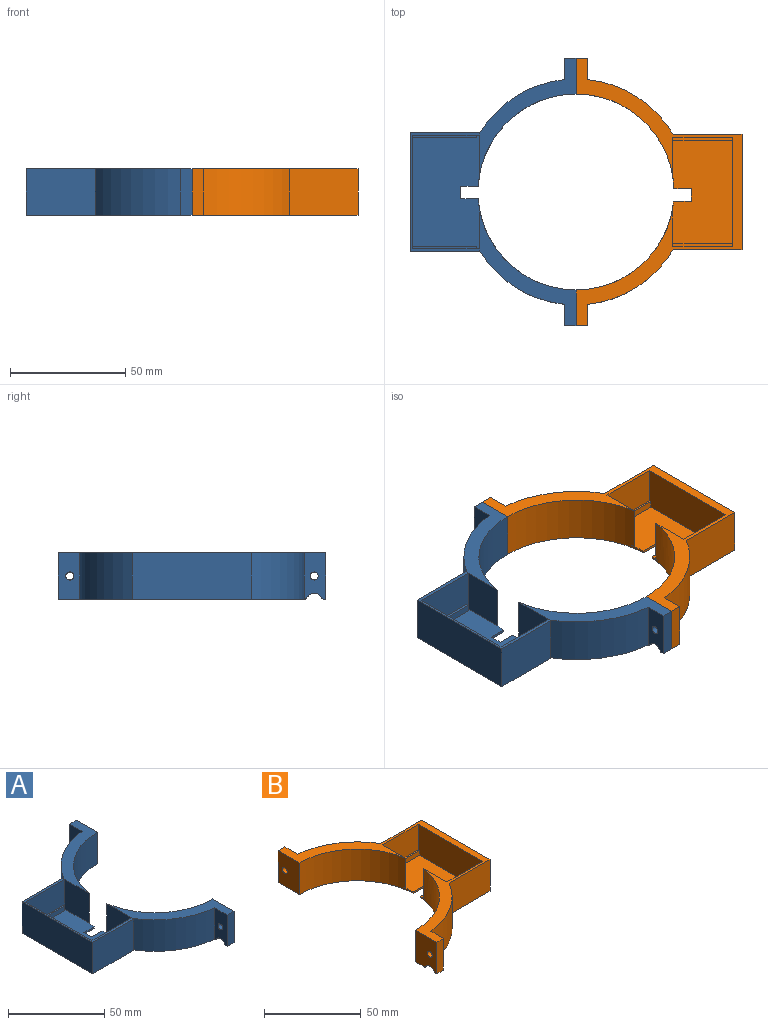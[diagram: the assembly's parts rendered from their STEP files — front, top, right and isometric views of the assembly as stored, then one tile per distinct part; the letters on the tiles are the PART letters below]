
ASSEMBLY  parts=2 mates=1
PART A: 38 faces, bbox 72x116x20 mm
  f0: plane 106.97x72mm, normal (0,0,-1), area 2259.8mm2, adj f1,f5,f6,f7,f8,f9,f10,f12
  f1: plane 20x9.26mm, normal (-1,0,0), area 163mm2, adj f0,f6,f11,f14,f32,f34,f35,f36
  f2: plane 49x29mm, normal (0,0,1), area 1319.7mm2, adj f3,f4,f5,f10,f20,f21,f22,f23
  f3: plane 49x19mm, normal (1,0,0), area 925mm2, adj f2,f4,f21,f27,f28,f30,f31,f32
  f4: plane 29x19mm, normal (0,-1,0), area 467mm2, adj f2,f3,f20,f26,f28,f32
  f5: cylinder r=42.5mm len=42.39mm, axis (0,0,1), area 1208.2mm2, adj f0,f2,f9,f22,f23,f32
  f6: cylinder r=49mm len=37mm, axis (0,0,1), area 908.9mm2, adj f0,f1,f15,f32
  f7: plane 20x15.5mm, normal (1,0,0), area 300.4mm2, adj f0,f10,f13,f32,f33
  f8: cylinder r=49mm len=37mm, axis (0,0,1), area 908.9mm2, adj f0,f12,f16,f32
  f9: plane 20x15.5mm, normal (1,0,0), area 287.9mm2, adj f0,f5,f11,f14,f32,f34,f35,f36
  f10: cylinder r=42.5mm len=42.43mm, axis (0,0,1), area 1208.7mm2, adj f0,f2,f7,f20,f24,f32
  f11: plane 5x0.97mm, normal (0,0,-1), area 4.8mm2, adj f1,f9,f14,f36
  f12: plane 20x9.26mm, normal (-1,0,0), area 175.5mm2, adj f0,f8,f13,f32,f33
  f13: plane 20x5mm, normal (0,1,0), area 100mm2, adj f0,f7,f12,f32
  f14: plane 20x5mm, normal (0,-1,0), area 100mm2, adj f1,f9,f11,f32
  f15: plane 20x0.76mm, normal (1,0,0), area 15.2mm2, adj f0,f6,f18,f32
  f16: plane 20x0.76mm, normal (1,0,0), area 15.2mm2, adj f0,f8,f19,f32
  f17: plane 52x20mm, normal (-1,0,0), area 1040mm2, adj f0,f18,f19,f32
  f18: plane 30x20mm, normal (0,-1,0), area 600mm2, adj f0,f15,f17,f32
  f19: plane 30x20mm, normal (0,1,0), area 600mm2, adj f0,f16,f17,f32
  f20: plane 19x18mm, normal (-1,0,0), area 342mm2, adj f2,f4,f10,f32
  f21: plane 29x19mm, normal (0,1,0), area 467mm2, adj f2,f3,f22,f29,f31,f32
  f22: plane 19x18mm, normal (-1,0,0), area 342mm2, adj f2,f5,f21,f32
  f23: plane 7.53x1mm, normal (0,1,0), area 7.5mm2, adj f0,f2,f5,f25
  f24: plane 7.5x1mm, normal (0,-1,0), area 7.5mm2, adj f0,f2,f10,f25
  f25: plane 5.5x1mm, normal (1,0,0), area 5.5mm2, adj f0,f2,f23,f24
  f26: plane 3x1mm, normal (1,0,0), area 3mm2, adj f2,f4,f27,f28
  f27: plane 28x3mm, normal (0,-1,0), area 84mm2, adj f2,f3,f26,f28
  f28: plane 28x1mm, normal (0,0,1), area 28mm2, adj f3,f4,f26,f27
  f29: plane 3x1mm, normal (1,0,0), area 3mm2, adj f2,f21,f30,f31
  f30: plane 28x3mm, normal (0,1,0), area 84mm2, adj f2,f3,f29,f31
  f31: plane 28x1mm, normal (0,0,1), area 28mm2, adj f3,f21,f29,f30
  f32: plane 116x72mm, normal (0,0,1), area 929.3mm2, adj f1,f3,f4,f5,f6,f7,f8,f9
  f33: cylinder r=1.75mm len=5mm, axis (-1,0,0), area 55mm2, adj f7,f12
  f34: cylinder r=1.75mm len=5mm, axis (-1,0,0), area 55mm2, adj f1,f9
  f35: cylinder r=3.5mm len=6.27mm, axis (1,0,0), area 38.9mm2, adj f1,f9,f36,f37
  f36: cylinder r=1mm len=5mm, axis (1,0,0), area 5.6mm2, adj f1,f9,f11,f35
  f37: cylinder r=1mm len=5mm, axis (1,0,0), area 5.6mm2, adj f0,f1,f9,f35
PART B: 34 faces, bbox 72x116x20 mm
  f0: plane 5x0.97mm, normal (0,0,-1), area 4.8mm2, adj f1,f8,f12,f33
  f1: plane 20x9.26mm, normal (1,0,0), area 163mm2, adj f0,f7,f11,f12,f25,f26,f31,f32
  f2: cylinder r=42.5mm len=42.47mm, axis (0,0,1), area 1209.7mm2, adj f5,f10,f11,f20,f25,f30
  f3: plane 26x16mm, normal (0,1,0), area 416mm2, adj f4,f18,f24,f25
  f4: plane 19x17mm, normal (1,0,0), area 320mm2, adj f3,f5,f6,f23,f24,f25
  f5: plane 45x26mm, normal (0,0,1), area 1124.1mm2, adj f2,f4,f6,f18,f20,f21,f23,f28
  f6: cylinder r=42.5mm len=42.31mm, axis (0,0,1), area 1207.2mm2, adj f4,f5,f8,f11,f25,f28
  f7: cylinder r=49mm len=37.14mm, axis (0,0,1), area 914.5mm2, adj f1,f11,f15,f25
  f8: plane 20x15.5mm, normal (-1,0,0), area 287.9mm2, adj f0,f6,f11,f12,f25,f26,f31,f32
  f9: cylinder r=49mm len=37.14mm, axis (0,0,1), area 914.5mm2, adj f11,f13,f17,f25
  f10: plane 20x15.5mm, normal (-1,0,0), area 300.4mm2, adj f2,f11,f14,f25,f27
  f11: plane 106.97x72mm, normal (0,0,-1), area 2199.3mm2, adj f1,f2,f6,f7,f8,f9,f10,f13
  f12: plane 20x5mm, normal (0,-1,0), area 100mm2, adj f0,f1,f8,f25
  f13: plane 20x9.26mm, normal (1,0,0), area 175.5mm2, adj f9,f11,f14,f25,f27
  f14: plane 20x5mm, normal (0,1,0), area 100mm2, adj f10,f11,f13,f25
  f15: plane 29.86x20mm, normal (0,-1,0), area 597.1mm2, adj f7,f11,f16,f25
  f16: plane 50x20mm, normal (1,0,0), area 1000mm2, adj f11,f15,f17,f25
  f17: plane 29.86x20mm, normal (0,1,0), area 597.1mm2, adj f9,f11,f16,f25
  f18: plane 47x19mm, normal (-1,0,0), area 887mm2, adj f3,f5,f19,f21,f22,f23,f24,f25
  f19: plane 26x16mm, normal (0,-1,0), area 416mm2, adj f18,f20,f22,f25
  f20: plane 19x17mm, normal (1,0,0), area 320mm2, adj f2,f5,f19,f21,f22,f25
  f21: plane 26x3mm, normal (0,-1,0), area 78mm2, adj f5,f18,f20,f22
  f22: plane 26x1mm, normal (0,0,1), area 26mm2, adj f18,f19,f20,f21
  f23: plane 26x3mm, normal (0,1,0), area 78mm2, adj f4,f5,f18,f24
  f24: plane 26x1mm, normal (0,0,1), area 26mm2, adj f3,f4,f18,f23
  f25: plane 116x72mm, normal (0,0,1), area 1068.3mm2, adj f1,f2,f3,f4,f6,f7,f8,f9
  f26: cylinder r=1.75mm len=5mm, axis (1,0,0), area 55mm2, adj f1,f8
  f27: cylinder r=1.75mm len=5mm, axis (1,0,0), area 55mm2, adj f10,f13
  f28: plane 7.69x1mm, normal (0,1,0), area 7.7mm2, adj f5,f6,f11,f29
  f29: plane 5.5x1mm, normal (-1,0,0), area 5.5mm2, adj f5,f11,f28,f30
  f30: plane 7.53x1mm, normal (0,-1,0), area 7.5mm2, adj f2,f5,f11,f29
  f31: cylinder r=3.5mm len=6.27mm, axis (-1,0,0), area 38.9mm2, adj f1,f8,f32,f33
  f32: cylinder r=1mm len=5mm, axis (-1,0,0), area 5.6mm2, adj f1,f8,f11,f31
  f33: cylinder r=1mm len=5mm, axis (-1,0,0), area 5.6mm2, adj f0,f1,f8,f31
PLACE A t=(-141.58,-62.6,-12.47)mm
PLACE B t=(-141.58,-62.6,-12.47)mm
MATE fastened B.f27 <-> A.f33  axis (-1,0,0) through (-141.58,-9.6,-2.47)mm
